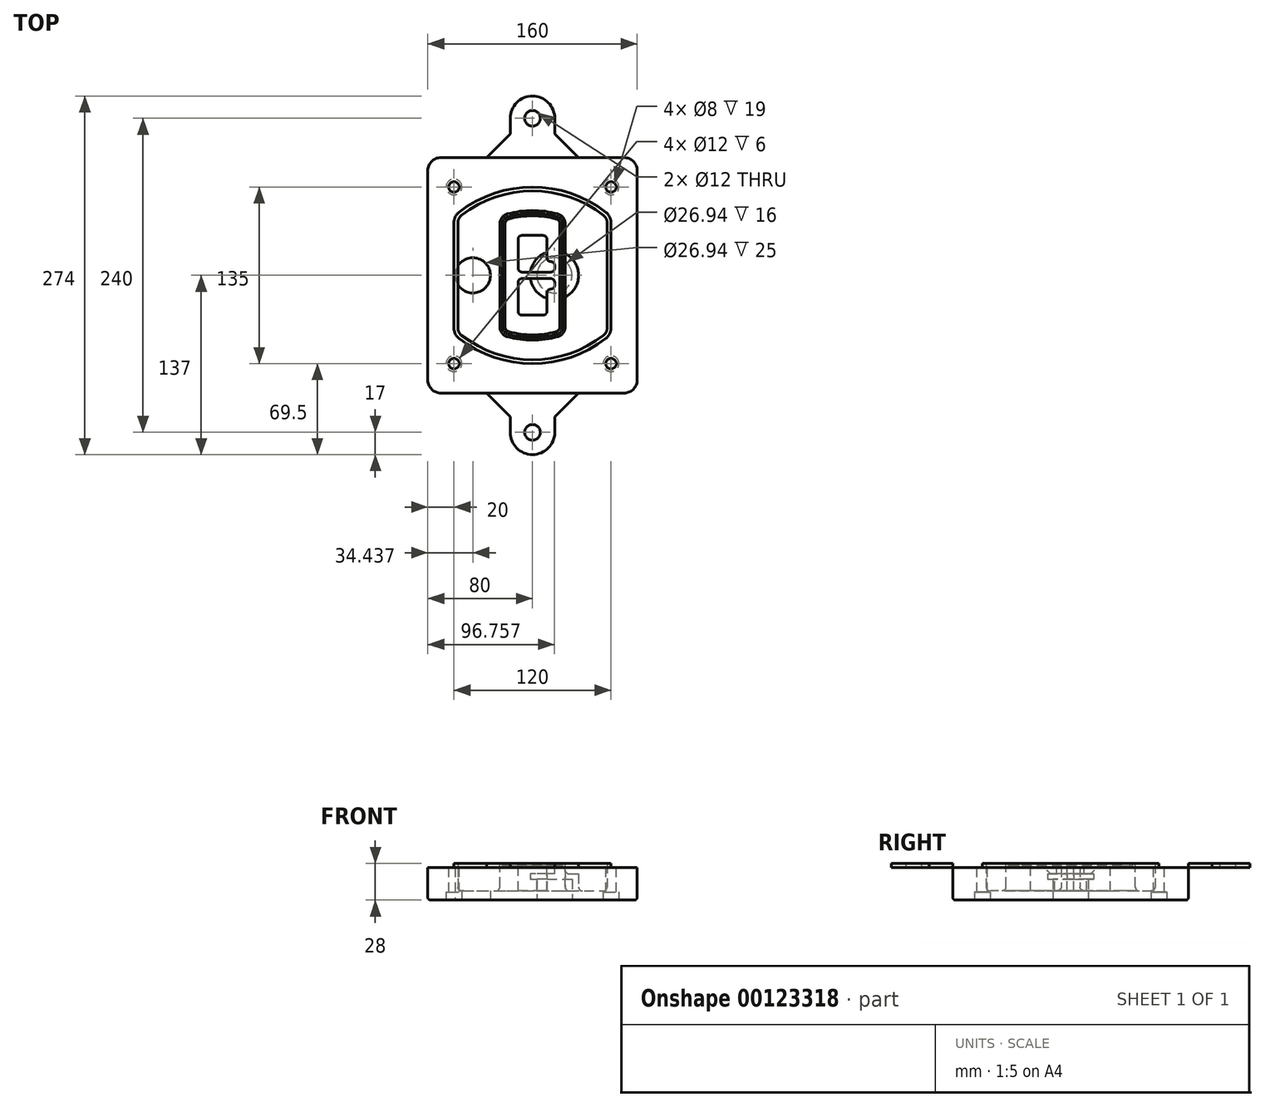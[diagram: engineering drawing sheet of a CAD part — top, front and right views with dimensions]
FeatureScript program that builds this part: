
annotation { "Feature Type Name" : "Feature", "Feature Type Description" : "" }
export const myFeature = defineFeature(function(context is Context, id is Id, definition is map)
    precondition{}
    {
        {
            var Q0;
            Q0=qCreatedBy(makeId("Top.planeOp"),FACE);
            var sketch = newSketch(context, id + "F0", { "sketchPlane" : qUnion([Q0])});
            skPoint(sketch, "E0.rect.middle", {"position": v(0, 0) * mm});
            skLineSegment(sketch, "E1.bottom", {"start": v(-70, -90) * mm, "end": v(70, -90) * mm});
            skLineSegment(sketch, "E1.top", {"start": v(-70, 90) * mm, "end": v(70, 90) * mm});
            skLineSegment(sketch, "E1.left", {"start": v(-80, -80) * mm, "end": v(-80, 80) * mm});
            skLineSegment(sketch, "E1.right", {"start": v(80, -80) * mm, "end": v(80, 80) * mm});
            skLineSegment(sketch, "E2", {"start": v(-80, 90) * mm, "end": v(80, -90) * mm, "construction": true});
            skLineSegment(sketch, "E3", {"start": v(80, 90) * mm, "end": v(-80, -90) * mm, "construction": true});
            skCircle(sketch, "E4", {"center": v(-60, 67.5) * mm, "radius": 4 * mm});
            skCircle(sketch, "E5", {"center": v(60, 67.5) * mm, "radius": 4 * mm});
            skCircle(sketch, "E6", {"center": v(60, -67.5) * mm, "radius": 4 * mm});
            skCircle(sketch, "E7", {"center": v(-60, -67.5) * mm, "radius": 4 * mm});
            skLineSegment(sketch, "E8", {"start": v(-60, 67.5) * mm, "end": v(60, 67.5) * mm, "construction": true});
            skLineSegment(sketch, "E9", {"start": v(60, 67.5) * mm, "end": v(60, -67.5) * mm, "construction": true});
            skLineSegment(sketch, "E10", {"start": v(60, -67.5) * mm, "end": v(-60, -67.5) * mm, "construction": true});
            skLineSegment(sketch, "E11", {"start": v(-60, -67.5) * mm, "end": v(-60, 67.5) * mm, "construction": true});
            skLineSegment(sketch, "E12", {"start": v(-60, 40.3) * mm, "end": v(-60, -40.3) * mm});
            skLineSegment(sketch, "E13", {"start": v(60, 40.3) * mm, "end": v(60, -40.3) * mm});
            skArc(sketch, "E14", {"start": v(56.15, 48.18) * mm, "mid": v(0, 67.5) * mm, "end": v(-56.15, 48.18) * mm});
            skArc(sketch, "E15", {"start": v(-56.15, -48.18) * mm, "mid": v(0, -67.5) * mm, "end": v(56.15, -48.18) * mm});
            skLineSegment(sketch, "E16", {"start": v(-60, 0) * mm, "end": v(60, 0) * mm, "construction": true});
            skPoint(sketch, "E17.visualSharp", {"position": v(-60, -45) * mm});
            skArc(sketch, "E17.filletArc", {"start": v(-60, -40.3) * mm, "mid": v(-58.99, -44.68) * mm, "end": v(-56.15, -48.18) * mm});
            skPoint(sketch, "E18.visualSharp", {"position": v(-60, 45) * mm});
            skArc(sketch, "E18.filletArc", {"start": v(-56.15, 48.18) * mm, "mid": v(-58.99, 44.68) * mm, "end": v(-60, 40.3) * mm});
            skPoint(sketch, "E19.visualSharp", {"position": v(60, 45) * mm});
            skArc(sketch, "E19.filletArc", {"start": v(60, 40.3) * mm, "mid": v(58.99, 44.68) * mm, "end": v(56.15, 48.18) * mm});
            skPoint(sketch, "E20.visualSharp", {"position": v(60, -45) * mm});
            skArc(sketch, "E20.filletArc", {"start": v(56.15, -48.18) * mm, "mid": v(58.99, -44.68) * mm, "end": v(60, -40.3) * mm});
            skPoint(sketch, "E21.visualSharp", {"position": v(-80, 90) * mm});
            skArc(sketch, "E21.filletArc", {"start": v(-70, 90) * mm, "mid": v(-77.07, 87.07) * mm, "end": v(-80, 80) * mm});
            skPoint(sketch, "E22.visualSharp", {"position": v(80, 90) * mm});
            skArc(sketch, "E22.filletArc", {"start": v(80, 80) * mm, "mid": v(77.07, 87.07) * mm, "end": v(70, 90) * mm});
            skPoint(sketch, "E23.visualSharp", {"position": v(80, -90) * mm});
            skArc(sketch, "E23.filletArc", {"start": v(70, -90) * mm, "mid": v(77.07, -87.07) * mm, "end": v(80, -80) * mm});
            skPoint(sketch, "E24.visualSharp", {"position": v(-80, -90) * mm});
            skArc(sketch, "E24.filletArc", {"start": v(-80, -80) * mm, "mid": v(-77.07, -87.07) * mm, "end": v(-70, -90) * mm});
            skArc(sketch, "E25.0", {"start": v(57, 40.3) * mm, "mid": v(56.3, 43.36) * mm, "end": v(54.3, 45.81) * mm});
            skLineSegment(sketch, "E25.1", {"start": v(57, 40.3) * mm, "end": v(57, -40.3) * mm});
            skArc(sketch, "E25.2", {"start": v(54.3, -45.81) * mm, "mid": v(56.3, -43.36) * mm, "end": v(57, -40.3) * mm});
            skArc(sketch, "E25.3", {"start": v(-54.3, -45.81) * mm, "mid": v(0, -64.5) * mm, "end": v(54.3, -45.81) * mm});
            skArc(sketch, "E25.4", {"start": v(-57, -40.3) * mm, "mid": v(-56.3, -43.36) * mm, "end": v(-54.3, -45.81) * mm});
            skArc(sketch, "E25.5", {"start": v(54.3, 45.81) * mm, "mid": v(0, 64.5) * mm, "end": v(-54.3, 45.81) * mm});
            skLineSegment(sketch, "E25.6", {"start": v(-57, 40.3) * mm, "end": v(-57, -40.3) * mm});
            skArc(sketch, "E25.7", {"start": v(-54.3, 45.81) * mm, "mid": v(-56.3, 43.36) * mm, "end": v(-57, 40.3) * mm});
            skArc(sketch, "E26.0", {"start": v(-58.62, 51.33) * mm, "mid": v(-62.58, 46.43) * mm, "end": v(-64, 40.3) * mm});
            skArc(sketch, "E26.1", {"start": v(58.62, 51.33) * mm, "mid": v(0, 71.5) * mm, "end": v(-58.62, 51.33) * mm});
            skArc(sketch, "E26.2", {"start": v(64, 40.3) * mm, "mid": v(62.58, 46.43) * mm, "end": v(58.62, 51.33) * mm});
            skLineSegment(sketch, "E26.3", {"start": v(64, 40.3) * mm, "end": v(64, -40.3) * mm});
            skArc(sketch, "E26.4", {"start": v(58.62, -51.33) * mm, "mid": v(62.58, -46.43) * mm, "end": v(64, -40.3) * mm});
            skLineSegment(sketch, "E26.5", {"start": v(-64, 40.3) * mm, "end": v(-64, -40.3) * mm});
            skArc(sketch, "E26.6", {"start": v(-58.62, -51.33) * mm, "mid": v(0, -71.5) * mm, "end": v(58.62, -51.33) * mm});
            skArc(sketch, "E26.7", {"start": v(-64, -40.3) * mm, "mid": v(-62.58, -46.43) * mm, "end": v(-58.62, -51.33) * mm});
            skSolve(sketch);
        }
        {
            var Q0;
            Q0=makeQuery(id+"F0.imprint","IMPRINT",FACE,{"disambiguationData":[TD([[makeQuery(id+"F0.imprint","IMPRINT",EDGE,{"derivedFrom":sQuery(id+"F0.wireOp",EDGE,"E1.bottom")}),1.0]])]});
            var Q1;
            Q1=makeQuery(id+"F0.imprint","IMPRINT",FACE,{"disambiguationData":[TD([[makeQuery(id+"F0.imprint","IMPRINT",EDGE,{"derivedFrom":sQuery(id+"F0.wireOp",EDGE,"E12")}),1.0]])]});
            var Q2;
            Q2=makeQuery(id+"F0.imprint","IMPRINT",FACE,{"disambiguationData":[TD([[makeQuery(id+"F0.imprint","IMPRINT",EDGE,{"derivedFrom":sQuery(id+"F0.wireOp",EDGE,"E25.0")}),1.0]])]});
            var Q3;
            Q3=makeQuery(id+"F0.imprint","IMPRINT",FACE,{"disambiguationData":[TD([[makeQuery(id+"F0.imprint","IMPRINT",EDGE,{"derivedFrom":sQuery(id+"F0.wireOp",EDGE,"E12")}),-1.0]])]});
            extrude(context, id + "F1", {"entities" : qUnion([Q0, Q1, Q2, Q3]), "oppositeDirection" : true, "depth" : 25 * mm});
        }
        {
            var Q0;
            Q0=makeQuery(id+"F0.imprint","IMPRINT",FACE,{"disambiguationData":[TD([[makeQuery(id+"F0.imprint","IMPRINT",EDGE,{"derivedFrom":sQuery(id+"F0.wireOp",EDGE,"E12")}),1.0]])]});
            extrude(context, id + "F2", {"entities" : qUnion([Q0]), "operationType" : NewBodyOperationType.ADD, "depth" : 3 * mm});
        }
        {
            var Q0;
            Q0=makeQuery(id+"F0.imprint","IMPRINT",FACE,{"disambiguationData":[TD([[makeQuery(id+"F0.imprint","IMPRINT",EDGE,{"derivedFrom":sQuery(id+"F0.wireOp",EDGE,"E25.0")}),1.0]])]});
            extrude(context, id + "F3", {"entities" : qUnion([Q0]), "operationType" : NewBodyOperationType.REMOVE, "oppositeDirection" : true, "depth" : 18 * mm});
        }
        {
            var Q0;
            Q0=makeQuery(id+"F2.opExtrude","CAP_FACE",FACE,{"disambiguationData":[OSD([sQuery(id+"F0.wireOp",EDGE,"E12"),sQuery(id+"F0.wireOp",EDGE,"E13"),sQuery(id+"F0.wireOp",EDGE,"E14"),sQuery(id+"F0.wireOp",EDGE,"E15"),sQuery(id+"F0.wireOp",EDGE,"E17.filletArc"),sQuery(id+"F0.wireOp",EDGE,"E18.filletArc"),sQuery(id+"F0.wireOp",EDGE,"E19.filletArc"),sQuery(id+"F0.wireOp",EDGE,"E20.filletArc"),sQuery(id+"F0.wireOp",EDGE,"E25.0"),sQuery(id+"F0.wireOp",EDGE,"E25.1"),sQuery(id+"F0.wireOp",EDGE,"E25.2"),sQuery(id+"F0.wireOp",EDGE,"E25.3"),sQuery(id+"F0.wireOp",EDGE,"E25.4"),sQuery(id+"F0.wireOp",EDGE,"E25.5"),sQuery(id+"F0.wireOp",EDGE,"E25.6"),sQuery(id+"F0.wireOp",EDGE,"E25.7")])],"isStart":false});
            var sketch = newSketch(context, id + "F4", { "sketchPlane" : qUnion([Q0])});
            skArc(sketch, "E27.0", {"start": v(-19.08, -46.97) * mm, "mid": v(0, -49.5) * mm, "end": v(19.08, -46.97) * mm});
            skArc(sketch, "E28.0", {"start": v(19.08, 46.97) * mm, "mid": v(0, 49.5) * mm, "end": v(-19.08, 46.97) * mm});
            skLineSegment(sketch, "E29", {"start": v(-25, 39.25) * mm, "end": v(-25, -39.25) * mm});
            skLineSegment(sketch, "E30", {"start": v(25, 39.25) * mm, "end": v(25, -39.25) * mm});
            skLineSegment(sketch, "E31", {"start": v(-25, 45.1) * mm, "end": v(25, 45.1) * mm, "construction": true});
            skLineSegment(sketch, "E32", {"start": v(-25, -45.1) * mm, "end": v(25, -45.1) * mm, "construction": true});
            skPoint(sketch, "E33.visualSharp", {"position": v(-25, 45.1) * mm});
            skArc(sketch, "E33.filletArc", {"start": v(-19.08, 46.97) * mm, "mid": v(-23.35, 44.11) * mm, "end": v(-25, 39.25) * mm});
            skPoint(sketch, "E34.visualSharp", {"position": v(25, 45.1) * mm});
            skArc(sketch, "E34.filletArc", {"start": v(25, 39.25) * mm, "mid": v(23.35, 44.11) * mm, "end": v(19.08, 46.97) * mm});
            skPoint(sketch, "E35.visualSharp", {"position": v(25, -45.1) * mm});
            skArc(sketch, "E35.filletArc", {"start": v(19.08, -46.97) * mm, "mid": v(23.35, -44.11) * mm, "end": v(25, -39.25) * mm});
            skPoint(sketch, "E36.visualSharp", {"position": v(-25, -45.1) * mm});
            skArc(sketch, "E36.filletArc", {"start": v(-25, -39.25) * mm, "mid": v(-23.35, -44.11) * mm, "end": v(-19.08, -46.97) * mm});
            skArc(sketch, "E37.0", {"start": v(54.3, 45.81) * mm, "mid": v(0, 64.5) * mm, "end": v(-54.3, 45.81) * mm});
            skArc(sketch, "E37.1", {"start": v(-54.3, 45.81) * mm, "mid": v(-56.3, 43.36) * mm, "end": v(-57, 40.3) * mm});
            skLineSegment(sketch, "E37.2", {"start": v(-57, 40.3) * mm, "end": v(-57, -40.3) * mm});
            skArc(sketch, "E37.3", {"start": v(-57, -40.3) * mm, "mid": v(-56.3, -43.36) * mm, "end": v(-54.3, -45.81) * mm});
            skArc(sketch, "E37.4", {"start": v(-54.3, -45.81) * mm, "mid": v(0, -64.5) * mm, "end": v(54.3, -45.81) * mm});
            skArc(sketch, "E37.5", {"start": v(54.3, -45.81) * mm, "mid": v(56.3, -43.36) * mm, "end": v(57, -40.3) * mm});
            skLineSegment(sketch, "E37.6", {"start": v(57, 40.3) * mm, "end": v(57, -40.3) * mm});
            skArc(sketch, "E37.7", {"start": v(57, 40.3) * mm, "mid": v(56.3, 43.36) * mm, "end": v(54.3, 45.81) * mm});
            skLineSegment(sketch, "E38.0", {"start": v(23, 39.25) * mm, "end": v(23, -39.25) * mm});
            skArc(sketch, "E38.1", {"start": v(18.56, -45.04) * mm, "mid": v(21.76, -42.9) * mm, "end": v(23, -39.25) * mm});
            skArc(sketch, "E38.2", {"start": v(-18.56, -45.04) * mm, "mid": v(0, -47.5) * mm, "end": v(18.56, -45.04) * mm});
            skArc(sketch, "E38.3", {"start": v(-23, -39.25) * mm, "mid": v(-21.76, -42.9) * mm, "end": v(-18.56, -45.04) * mm});
            skLineSegment(sketch, "E38.4", {"start": v(-23, 39.25) * mm, "end": v(-23, -39.25) * mm});
            skArc(sketch, "E38.5", {"start": v(23, 39.25) * mm, "mid": v(21.76, 42.9) * mm, "end": v(18.56, 45.04) * mm});
            skArc(sketch, "E38.6", {"start": v(-18.56, 45.04) * mm, "mid": v(-21.76, 42.9) * mm, "end": v(-23, 39.25) * mm});
            skArc(sketch, "E38.7", {"start": v(18.56, 45.04) * mm, "mid": v(0, 47.5) * mm, "end": v(-18.56, 45.04) * mm});
            skArc(sketch, "E39.0", {"start": v(21, 39.25) * mm, "mid": v(20.18, 41.68) * mm, "end": v(18.04, 43.1) * mm});
            skLineSegment(sketch, "E39.1", {"start": v(21, 39.25) * mm, "end": v(21, -39.25) * mm});
            skArc(sketch, "E39.2", {"start": v(18.04, -43.1) * mm, "mid": v(20.18, -41.68) * mm, "end": v(21, -39.25) * mm});
            skArc(sketch, "E39.3", {"start": v(-18.04, -43.1) * mm, "mid": v(0, -45.5) * mm, "end": v(18.04, -43.1) * mm});
            skArc(sketch, "E39.4", {"start": v(-21, -39.25) * mm, "mid": v(-20.18, -41.68) * mm, "end": v(-18.04, -43.1) * mm});
            skArc(sketch, "E39.5", {"start": v(18.04, 43.1) * mm, "mid": v(0, 45.5) * mm, "end": v(-18.04, 43.1) * mm});
            skLineSegment(sketch, "E39.6", {"start": v(-21, 39.25) * mm, "end": v(-21, -39.25) * mm});
            skArc(sketch, "E39.7", {"start": v(-18.04, 43.1) * mm, "mid": v(-20.18, 41.68) * mm, "end": v(-21, 39.25) * mm});
            skLineSegment(sketch, "E40", {"start": v(-25, 0) * mm, "end": v(25, 0) * mm, "construction": true});
            skLineSegment(sketch, "E41", {"start": v(-11, 5.5) * mm, "end": v(-11, 27.5) * mm});
            skLineSegment(sketch, "E42", {"start": v(-8, 30.5) * mm, "end": v(8, 30.5) * mm});
            skLineSegment(sketch, "E43", {"start": v(11, 27.5) * mm, "end": v(11, 13.5) * mm});
            skLineSegment(sketch, "E44", {"start": v(14, 10.5) * mm, "end": v(14, 10.5) * mm});
            skLineSegment(sketch, "E45", {"start": v(17, 7.5) * mm, "end": v(17, 5.5) * mm});
            skLineSegment(sketch, "E46", {"start": v(14, 2.5) * mm, "end": v(-8, 2.5) * mm});
            skPoint(sketch, "E47.visualSharp", {"position": v(-11, 30.5) * mm});
            skArc(sketch, "E47.filletArc", {"start": v(-8, 30.5) * mm, "mid": v(-10.12, 29.62) * mm, "end": v(-11, 27.5) * mm});
            skPoint(sketch, "E48.visualSharp", {"position": v(11, 30.5) * mm});
            skArc(sketch, "E48.filletArc", {"start": v(11, 27.5) * mm, "mid": v(10.12, 29.62) * mm, "end": v(8, 30.5) * mm});
            skPoint(sketch, "E49.visualSharp", {"position": v(11, 10.5) * mm});
            skArc(sketch, "E49.filletArc", {"start": v(11, 13.5) * mm, "mid": v(11.88, 11.38) * mm, "end": v(14, 10.5) * mm});
            skPoint(sketch, "E50.visualSharp", {"position": v(17, 10.5) * mm});
            skArc(sketch, "E50.filletArc", {"start": v(17, 7.5) * mm, "mid": v(16.12, 9.62) * mm, "end": v(14, 10.5) * mm});
            skPoint(sketch, "E51.visualSharp", {"position": v(17, 2.5) * mm});
            skArc(sketch, "E51.filletArc", {"start": v(14, 2.5) * mm, "mid": v(16.12, 3.38) * mm, "end": v(17, 5.5) * mm});
            skPoint(sketch, "E52.visualSharp", {"position": v(-11, 2.5) * mm});
            skArc(sketch, "E52.filletArc", {"start": v(-11, 5.5) * mm, "mid": v(-10.12, 3.38) * mm, "end": v(-8, 2.5) * mm});
            skLineSegment(sketch, "E53.0.MirrorCS", {"start": v(14, -2.5) * mm, "end": v(-8, -2.5) * mm});
            skArc(sketch, "E54.0.MirrorCS", {"start": v(-11, -5.5) * mm, "mid": v(-10.12, -3.38) * mm, "end": v(-8, -2.5) * mm});
            skLineSegment(sketch, "E55.0.MirrorCS", {"start": v(-11, -5.5) * mm, "end": v(-11, -27.5) * mm});
            skArc(sketch, "E56.0.MirrorCS", {"start": v(-8, -30.5) * mm, "mid": v(-10.12, -29.62) * mm, "end": v(-11, -27.5) * mm});
            skLineSegment(sketch, "E57.0.MirrorCS", {"start": v(-8, -30.5) * mm, "end": v(8, -30.5) * mm});
            skArc(sketch, "E58.0.MirrorCS", {"start": v(11, -27.5) * mm, "mid": v(10.12, -29.62) * mm, "end": v(8, -30.5) * mm});
            skLineSegment(sketch, "E59.0.MirrorCS", {"start": v(11, -27.5) * mm, "end": v(11, -13.5) * mm});
            skArc(sketch, "E60.0.MirrorCS", {"start": v(11, -13.5) * mm, "mid": v(11.88, -11.38) * mm, "end": v(14, -10.5) * mm});
            skArc(sketch, "E61.0.MirrorCS", {"start": v(17, -7.5) * mm, "mid": v(16.12, -9.62) * mm, "end": v(14, -10.5) * mm});
            skLineSegment(sketch, "E62.0.MirrorCS", {"start": v(17, -7.5) * mm, "end": v(17, -5.5) * mm});
            skArc(sketch, "E63.0.MirrorCS", {"start": v(14, -2.5) * mm, "mid": v(16.12, -3.38) * mm, "end": v(17, -5.5) * mm});
            skSolve(sketch);
        }
        {
            var Q0;
            Q0=makeQuery(id+"F4.imprint","IMPRINT",FACE,{"disambiguationData":[TD([[makeQuery(id+"F4.imprint","IMPRINT",EDGE,{"derivedFrom":sQuery(id+"F4.wireOp",EDGE,"E27.0")}),1.0]])]});
            var Q1;
            Q1=makeQuery(id+"F4.imprint","IMPRINT",FACE,{"disambiguationData":[TD([[makeQuery(id+"F4.imprint","IMPRINT",EDGE,{"derivedFrom":sQuery(id+"F4.wireOp",EDGE,"E38.0")}),-1.0]])]});
            var Q2;
            Q2=makeQuery(id+"F4.imprint","IMPRINT",FACE,{"disambiguationData":[TD([[makeQuery(id+"F4.imprint","IMPRINT",EDGE,{"derivedFrom":sQuery(id+"F4.wireOp",EDGE,"E39.0")}),1.0]])]});
            extrude(context, id + "F5", {"entities" : qUnion([Q0, Q1, Q2]), "operationType" : NewBodyOperationType.ADD, "endBound" : BoundingType.UP_TO_NEXT, "oppositeDirection" : true, "depth" : 25 * mm});
        }
        {
            var Q0;
            Q0=makeQuery(id+"F4.imprint","IMPRINT",FACE,{"disambiguationData":[TD([[makeQuery(id+"F4.imprint","IMPRINT",EDGE,{"derivedFrom":sQuery(id+"F4.wireOp",EDGE,"E38.0")}),-1.0]])]});
            extrude(context, id + "F6", {"entities" : qUnion([Q0]), "operationType" : NewBodyOperationType.REMOVE, "oppositeDirection" : true, "depth" : 2 * mm});
        }
        {
            var Q0;
            Q0=makeQuery(id+"F1.opExtrude","CAP_FACE",FACE,{"disambiguationData":[OSD([sQuery(id+"F0.wireOp",EDGE,"E1.bottom"),sQuery(id+"F0.wireOp",EDGE,"E1.top"),sQuery(id+"F0.wireOp",EDGE,"E1.left"),sQuery(id+"F0.wireOp",EDGE,"E1.right"),sQuery(id+"F0.wireOp",EDGE,"E4"),sQuery(id+"F0.wireOp",EDGE,"E5"),sQuery(id+"F0.wireOp",EDGE,"E6"),sQuery(id+"F0.wireOp",EDGE,"E7"),sQuery(id+"F0.wireOp",EDGE,"E21.filletArc"),sQuery(id+"F0.wireOp",EDGE,"E22.filletArc"),sQuery(id+"F0.wireOp",EDGE,"E23.filletArc"),sQuery(id+"F0.wireOp",EDGE,"E24.filletArc")])],"isStart":false});
            var sketch = newSketch(context, id + "F7", { "sketchPlane" : qUnion([Q0])});
            skCircle(sketch, "E64", {"center": v(16.76, 0) * mm, "radius": 13.47 * mm});
            skCircle(sketch, "E65", {"center": v(-45.56, 0) * mm, "radius": 13.47 * mm});
            skLineSegment(sketch, "E66", {"start": v(80, 0) * mm, "end": v(-80, 0) * mm});
            skCircle(sketch, "E67", {"center": v(16.76, 0) * mm, "radius": 18.47 * mm});
            skCircle(sketch, "E68", {"center": v(60, -67.5) * mm, "radius": 6 * mm});
            skCircle(sketch, "E69", {"center": v(-60, -67.5) * mm, "radius": 6 * mm});
            skCircle(sketch, "E70", {"center": v(-60, 67.5) * mm, "radius": 6 * mm});
            skCircle(sketch, "E71", {"center": v(60, 67.5) * mm, "radius": 6 * mm});
            skSolve(sketch);
        }
        {
            var Q0;
            {var subQ1=sQuery(id+"F7.wireOp",EDGE,"E66");var subQ4=sQuery(id+"F7.wireOp",EDGE,"E64");var subQ6=makeQuery(id+"F7.imprint","INTERSECT",VERTEX,{"disambiguationData":[OD(0.0)],"derivedFrom":[subQ4,subQ1]});Q0=makeQuery(id+"F7.imprint","IMPRINT",FACE,{"disambiguationData":[TD([[makeQuery(id+"F7.imprint","IMPRINT",EDGE,{"disambiguationData":[TD([[subQ6,-1.0]])],"derivedFrom":subQ4}),-1.0]])]});}
            var Q1;
            {var subQ0=sQuery(id+"F7.wireOp",EDGE,"E66");var subQ1=sQuery(id+"F7.wireOp",EDGE,"E64");var subQ3=makeQuery(id+"F7.imprint","INTERSECT",VERTEX,{"disambiguationData":[OD(0.0)],"derivedFrom":[subQ1,subQ0]});Q1=makeQuery(id+"F7.imprint","IMPRINT",FACE,{"disambiguationData":[TD([[makeQuery(id+"F7.imprint","IMPRINT",EDGE,{"disambiguationData":[TD([[subQ3,-1.0]])],"derivedFrom":subQ1}),1.0]])]});}
            var Q2;
            {var subQ0=sQuery(id+"F7.wireOp",EDGE,"E66");var subQ1=sQuery(id+"F7.wireOp",EDGE,"E64");var subQ3=makeQuery(id+"F7.imprint","INTERSECT",VERTEX,{"disambiguationData":[OD(0.0)],"derivedFrom":[subQ1,subQ0]});Q2=makeQuery(id+"F7.imprint","IMPRINT",FACE,{"disambiguationData":[TD([[makeQuery(id+"F7.imprint","IMPRINT",EDGE,{"disambiguationData":[TD([[subQ3,1.0]])],"derivedFrom":subQ1}),1.0]])]});}
            var Q3;
            {var subQ1=sQuery(id+"F7.wireOp",EDGE,"E66");var subQ4=sQuery(id+"F7.wireOp",EDGE,"E64");var subQ6=makeQuery(id+"F7.imprint","INTERSECT",VERTEX,{"disambiguationData":[OD(0.0)],"derivedFrom":[subQ4,subQ1]});Q3=makeQuery(id+"F7.imprint","IMPRINT",FACE,{"disambiguationData":[TD([[makeQuery(id+"F7.imprint","IMPRINT",EDGE,{"disambiguationData":[TD([[subQ6,1.0]])],"derivedFrom":subQ4}),-1.0]])]});}
            extrude(context, id + "F8", {"entities" : qUnion([Q0, Q1, Q2, Q3]), "operationType" : NewBodyOperationType.ADD, "oppositeDirection" : true, "depth" : 20 * mm});
        }
        {
            var Q0;
            {var subQ0=sQuery(id+"F7.wireOp",EDGE,"E66");var subQ1=sQuery(id+"F7.wireOp",EDGE,"E64");var subQ3=makeQuery(id+"F7.imprint","INTERSECT",VERTEX,{"disambiguationData":[OD(0.0)],"derivedFrom":[subQ1,subQ0]});Q0=makeQuery(id+"F7.imprint","IMPRINT",FACE,{"disambiguationData":[TD([[makeQuery(id+"F7.imprint","IMPRINT",EDGE,{"disambiguationData":[TD([[subQ3,-1.0]])],"derivedFrom":subQ1}),1.0]])]});}
            var Q1;
            {var subQ0=sQuery(id+"F7.wireOp",EDGE,"E66");var subQ1=sQuery(id+"F7.wireOp",EDGE,"E64");var subQ3=makeQuery(id+"F7.imprint","INTERSECT",VERTEX,{"disambiguationData":[OD(0.0)],"derivedFrom":[subQ1,subQ0]});Q1=makeQuery(id+"F7.imprint","IMPRINT",FACE,{"disambiguationData":[TD([[makeQuery(id+"F7.imprint","IMPRINT",EDGE,{"disambiguationData":[TD([[subQ3,1.0]])],"derivedFrom":subQ1}),1.0]])]});}
            extrude(context, id + "F9", {"entities" : qUnion([Q0, Q1]), "operationType" : NewBodyOperationType.REMOVE, "oppositeDirection" : true, "depth" : 16 * mm});
        }
        {
            var Q0;
            {var subQ0=sQuery(id+"F7.wireOp",EDGE,"E66");var subQ1=sQuery(id+"F7.wireOp",EDGE,"E65");var subQ3=makeQuery(id+"F7.imprint","INTERSECT",VERTEX,{"disambiguationData":[OD(0.0)],"derivedFrom":[subQ1,subQ0]});Q0=makeQuery(id+"F7.imprint","IMPRINT",FACE,{"disambiguationData":[TD([[makeQuery(id+"F7.imprint","IMPRINT",EDGE,{"disambiguationData":[TD([[subQ3,-1.0]])],"derivedFrom":subQ1}),1.0]])]});}
            var Q1;
            {var subQ0=sQuery(id+"F7.wireOp",EDGE,"E66");var subQ1=sQuery(id+"F7.wireOp",EDGE,"E65");var subQ3=makeQuery(id+"F7.imprint","INTERSECT",VERTEX,{"disambiguationData":[OD(0.0)],"derivedFrom":[subQ1,subQ0]});Q1=makeQuery(id+"F7.imprint","IMPRINT",FACE,{"disambiguationData":[TD([[makeQuery(id+"F7.imprint","IMPRINT",EDGE,{"disambiguationData":[TD([[subQ3,1.0]])],"derivedFrom":subQ1}),1.0]])]});}
            extrude(context, id + "F10", {"entities" : qUnion([Q0, Q1]), "operationType" : NewBodyOperationType.REMOVE, "oppositeDirection" : true, "depth" : 25 * mm});
        }
        {
            var Q0;
            Q0=makeQuery(id+"F7.imprint","IMPRINT",FACE,{"disambiguationData":[TD([[makeQuery(id+"F7.imprint","IMPRINT",EDGE,{"derivedFrom":sQuery(id+"F7.wireOp",EDGE,"E68")}),1.0]])]});
            var Q1;
            Q1=makeQuery(id+"F7.imprint","IMPRINT",FACE,{"disambiguationData":[TD([[makeQuery(id+"F7.imprint","IMPRINT",EDGE,{"derivedFrom":makeQuery(id+"F1.opExtrude","CAP_EDGE",EDGE,{"disambiguationData":[OSD([sQuery(id+"F0.wireOp",EDGE,"E5")])],"isStart":false})}),-1.0]])]});
            var Q2;
            Q2=makeQuery(id+"F7.imprint","IMPRINT",FACE,{"disambiguationData":[TD([[makeQuery(id+"F7.imprint","IMPRINT",EDGE,{"derivedFrom":sQuery(id+"F7.wireOp",EDGE,"E69")}),1.0]])]});
            var Q3;
            Q3=makeQuery(id+"F7.imprint","IMPRINT",FACE,{"disambiguationData":[TD([[makeQuery(id+"F7.imprint","IMPRINT",EDGE,{"derivedFrom":makeQuery(id+"F1.opExtrude","CAP_EDGE",EDGE,{"disambiguationData":[OSD([sQuery(id+"F0.wireOp",EDGE,"E4")])],"isStart":false})}),-1.0]])]});
            var Q4;
            Q4=makeQuery(id+"F7.imprint","IMPRINT",FACE,{"disambiguationData":[TD([[makeQuery(id+"F7.imprint","IMPRINT",EDGE,{"derivedFrom":sQuery(id+"F7.wireOp",EDGE,"E70")}),1.0]])]});
            var Q5;
            Q5=makeQuery(id+"F7.imprint","IMPRINT",FACE,{"disambiguationData":[TD([[makeQuery(id+"F7.imprint","IMPRINT",EDGE,{"derivedFrom":makeQuery(id+"F1.opExtrude","CAP_EDGE",EDGE,{"disambiguationData":[OSD([sQuery(id+"F0.wireOp",EDGE,"E7")])],"isStart":false})}),-1.0]])]});
            var Q6;
            Q6=makeQuery(id+"F7.imprint","IMPRINT",FACE,{"disambiguationData":[TD([[makeQuery(id+"F7.imprint","IMPRINT",EDGE,{"derivedFrom":sQuery(id+"F7.wireOp",EDGE,"E71")}),1.0]])]});
            var Q7;
            Q7=makeQuery(id+"F7.imprint","IMPRINT",FACE,{"disambiguationData":[TD([[makeQuery(id+"F7.imprint","IMPRINT",EDGE,{"derivedFrom":makeQuery(id+"F1.opExtrude","CAP_EDGE",EDGE,{"disambiguationData":[OSD([sQuery(id+"F0.wireOp",EDGE,"E6")])],"isStart":false})}),-1.0]])]});
            extrude(context, id + "F11", {"entities" : qUnion([Q0, Q1, Q2, Q3, Q4, Q5, Q6, Q7]), "operationType" : NewBodyOperationType.REMOVE, "oppositeDirection" : true, "depth" : 6 * mm});
        }
        {
            var Q0;
            Q0=makeQuery(id+"F9.boolean.opBoolean","COPY",FACE,{"derivedFrom":makeQuery(id+"F9.opExtrude","CAP_FACE",FACE,{"disambiguationData":[OSD([sQuery(id+"F7.wireOp",EDGE,"E64")])],"isStart":false})});
            var sketch = newSketch(context, id + "F12", { "sketchPlane" : qUnion([Q0])});
            skArc(sketch, "E72.0", {"start": v(11, 17.55) * mm, "mid": v(2.57, 11.82) * mm, "end": v(-1.54, 2.5) * mm});
            skArc(sketch, "E72.1", {"start": v(-1.54, -2.5) * mm, "mid": v(2.57, -11.82) * mm, "end": v(11, -17.55) * mm});
            skLineSegment(sketch, "E73", {"start": v(-1.54, -2.5) * mm, "end": v(14, -2.5) * mm});
            skLineSegment(sketch, "E74.0", {"start": v(14, 2.5) * mm, "end": v(-1.54, 2.5) * mm});
            skArc(sketch, "E74.1", {"start": v(14, 2.5) * mm, "mid": v(16.12, 3.38) * mm, "end": v(17, 5.5) * mm});
            skLineSegment(sketch, "E74.2", {"start": v(17, 7.5) * mm, "end": v(17, 5.5) * mm});
            skArc(sketch, "E74.3", {"start": v(17, 7.5) * mm, "mid": v(16.12, 9.62) * mm, "end": v(14, 10.5) * mm});
            skArc(sketch, "E74.4", {"start": v(11, 13.5) * mm, "mid": v(11.88, 11.38) * mm, "end": v(14, 10.5) * mm});
            skLineSegment(sketch, "E74.5", {"start": v(11, 17.55) * mm, "end": v(11, 13.5) * mm});
            skLineSegment(sketch, "E74.7", {"start": v(14, -2.5) * mm, "end": v(-1.54, -2.5) * mm});
            skArc(sketch, "E74.8", {"start": v(14, -2.5) * mm, "mid": v(16.12, -3.38) * mm, "end": v(17, -5.5) * mm});
            skLineSegment(sketch, "E74.9", {"start": v(17, -7.5) * mm, "end": v(17, -5.5) * mm});
            skArc(sketch, "E74.10", {"start": v(17, -7.5) * mm, "mid": v(16.12, -9.62) * mm, "end": v(14, -10.5) * mm});
            skArc(sketch, "E74.11", {"start": v(11, -13.5) * mm, "mid": v(11.88, -11.38) * mm, "end": v(14, -10.5) * mm});
            skLineSegment(sketch, "E74.12", {"start": v(11, -17.55) * mm, "end": v(11, -13.5) * mm});
            skPoint(sketch, "E75.orphan", {"position": v(11, -27.5) * mm});
            skPoint(sketch, "E76.orphan", {"position": v(-8, -2.5) * mm});
            skPoint(sketch, "E77.orphan", {"position": v(-8, 2.5) * mm});
            skPoint(sketch, "E78.orphan", {"position": v(11, 27.5) * mm});
            skSolve(sketch);
        }
        {
            var Q0;
            {var subQ7=sQuery(id+"F12.wireOp",EDGE,"E72.0");var subQ14=sQuery(id+"F12.wireOp",EDGE,"E72.1");var subQ16=sQuery(id+"F12.wireOp",EDGE,"E74.1");var subQ18=sQuery(id+"F12.wireOp",EDGE,"E74.8");Q0=qUnion([makeQuery(id+"F12.imprint","IMPRINT",FACE,{"disambiguationData":[TD([[makeQuery(id+"F12.imprint","IMPRINT",EDGE,{"derivedFrom":subQ7}),1.0]])]}),makeQuery(id+"F12.imprint","IMPRINT",FACE,{"disambiguationData":[TD([[makeQuery(id+"F12.imprint","IMPRINT",EDGE,{"derivedFrom":subQ14}),1.0]])]}),makeQuery(id+"F12.imprint","IMPRINT",FACE,{"disambiguationData":[TD([[makeQuery(id+"F12.imprint","IMPRINT",EDGE,{"derivedFrom":subQ16}),1.0]])]}),makeQuery(id+"F12.imprint","IMPRINT",FACE,{"disambiguationData":[TD([[makeQuery(id+"F12.imprint","IMPRINT",EDGE,{"derivedFrom":subQ18}),-1.0]])]})]);}
            var Q1;
            Q1=makeQuery(id+"F5.boolean.opBoolean","SPLIT",FACE,{"disambiguationData":[TD([makeQuery(id+"F5.opExtrude","SWEPT_FACE",FACE,{"disambiguationData":[OSD([sQuery(id+"F4.wireOp",EDGE,"E41")])]})])],"derivedFrom":makeQuery(id+"F3.boolean.opBoolean","COPY",FACE,{"derivedFrom":makeQuery(id+"F3.opExtrude","CAP_FACE",FACE,{"disambiguationData":[OSD([sQuery(id+"F0.wireOp",EDGE,"E25.0"),sQuery(id+"F0.wireOp",EDGE,"E25.1"),sQuery(id+"F0.wireOp",EDGE,"E25.2"),sQuery(id+"F0.wireOp",EDGE,"E25.3"),sQuery(id+"F0.wireOp",EDGE,"E25.4"),sQuery(id+"F0.wireOp",EDGE,"E25.5"),sQuery(id+"F0.wireOp",EDGE,"E25.6"),sQuery(id+"F0.wireOp",EDGE,"E25.7")])],"isStart":false})})});
            extrude(context, id + "F13", {"entities" : qUnion([Q0]), "operationType" : NewBodyOperationType.REMOVE, "endBound" : BoundingType.UP_TO_SURFACE, "endBoundEntityFace" : qUnion([Q1]), "depth" : 25 * mm});
        }
        {
            var Q0;
            Q0=makeQuery(id+"F3.boolean.opBoolean","COPY",EDGE,{"derivedFrom":makeQuery(id+"F3.opExtrude","CAP_EDGE",EDGE,{"disambiguationData":[OSD([sQuery(id+"F0.wireOp",EDGE,"E25.6")])],"isStart":false})});
            var Q1;
            Q1=makeQuery(id+"F8.boolean.opBoolean","INTERSECT",EDGE,{"derivedFrom":[makeQuery(id+"F5.opExtrude","SWEPT_FACE",FACE,{"disambiguationData":[OSD([sQuery(id+"F4.wireOp",EDGE,"E30")])]}),makeQuery(id+"F8.opExtrude","CAP_FACE",FACE,{"disambiguationData":[OSD([sQuery(id+"F7.wireOp",EDGE,"E67")])],"isStart":false})]});
            var Q2;
            Q2=makeQuery(id+"F8.boolean.opBoolean","INTERSECT",EDGE,{"disambiguationData":[OD(1.0)],"derivedFrom":[makeQuery(id+"F5.opExtrude","SWEPT_FACE",FACE,{"disambiguationData":[OSD([sQuery(id+"F4.wireOp",EDGE,"E30")])]}),makeQuery(id+"F8.opExtrude","SWEPT_FACE",FACE,{"disambiguationData":[OSD([sQuery(id+"F7.wireOp",EDGE,"E67")])]})]});
            var Q3;
            {var subQ0=sQuery(id+"F4.wireOp",EDGE,"E30");Q3=makeQuery(id+"F8.boolean.opBoolean","SPLIT",EDGE,{"disambiguationData":[TD([makeQuery(id+"F5.opExtrude","SWEPT_FACE",FACE,{"disambiguationData":[OSD([sQuery(id+"F4.wireOp",EDGE,"E35.filletArc")])]})])],"derivedFrom":makeQuery(id+"F5.opExtrude","CAP_EDGE",EDGE,{"disambiguationData":[OSD([subQ0])],"isStart":false})});}
            var Q4;
            {var subQ0=sQuery(id+"F0.wireOp",EDGE,"E25.7");var subQ1=sQuery(id+"F0.wireOp",EDGE,"E25.1");var subQ2=sQuery(id+"F0.wireOp",EDGE,"E25.6");var subQ3=sQuery(id+"F0.wireOp",EDGE,"E25.5");var subQ4=sQuery(id+"F0.wireOp",EDGE,"E25.4");var subQ5=sQuery(id+"F0.wireOp",EDGE,"E25.0");var subQ6=sQuery(id+"F0.wireOp",EDGE,"E25.2");var subQ7=sQuery(id+"F0.wireOp",EDGE,"E25.3");Q4=makeQuery(id+"F8.boolean.opBoolean","INTERSECT",EDGE,{"derivedFrom":[makeQuery(id+"F5.boolean.opBoolean","SPLIT",FACE,{"disambiguationData":[TD([makeQuery(id+"F2.opExtrude","SWEPT_FACE",FACE,{"disambiguationData":[OSD([subQ5])]})])],"derivedFrom":makeQuery(id+"F3.boolean.opBoolean","COPY",FACE,{"derivedFrom":makeQuery(id+"F3.opExtrude","CAP_FACE",FACE,{"disambiguationData":[OSD([subQ5,subQ1,subQ6,subQ7,subQ4,subQ3,subQ2,subQ0])],"isStart":false})})}),makeQuery(id+"F8.opExtrude","SWEPT_FACE",FACE,{"disambiguationData":[OSD([sQuery(id+"F7.wireOp",EDGE,"E67")])]})]});}
            var Q5;
            Q5=makeQuery(id+"F8.boolean.opBoolean","INTERSECT",EDGE,{"disambiguationData":[OD(0.0)],"derivedFrom":[makeQuery(id+"F5.opExtrude","SWEPT_FACE",FACE,{"disambiguationData":[OSD([sQuery(id+"F4.wireOp",EDGE,"E30")])]}),makeQuery(id+"F8.opExtrude","SWEPT_FACE",FACE,{"disambiguationData":[OSD([sQuery(id+"F7.wireOp",EDGE,"E67")])]})]});
            fillet(context, id + "F14", {"entities" : qUnion([Q0, Q1, Q2, Q3, Q4, Q5]), "radius" : 3 * mm, "tangentPropagation" : true, "allowEdgeOverflow" : false});
        }
        {
            var Q0;
            Q0=makeQuery(id+"F1.opExtrude","CAP_EDGE",EDGE,{"disambiguationData":[OSD([sQuery(id+"F0.wireOp",EDGE,"E1.bottom")])],"isStart":false});
            fillet(context, id + "F15", {"entities" : qUnion([Q0]), "radius" : 2 * mm, "tangentPropagation" : true, "allowEdgeOverflow" : false});
        }
        {
            var Q0;
            {var subQ0=sQuery(id+"F0.wireOp",EDGE,"E22.filletArc");var subQ1=sQuery(id+"F0.wireOp",EDGE,"E7");var subQ2=sQuery(id+"F0.wireOp",EDGE,"E6");var subQ3=sQuery(id+"F0.wireOp",EDGE,"E5");var subQ4=sQuery(id+"F0.wireOp",EDGE,"E4");var subQ5=sQuery(id+"F0.wireOp",EDGE,"E1.bottom");var subQ6=sQuery(id+"F0.wireOp",EDGE,"E21.filletArc");var subQ7=sQuery(id+"F0.wireOp",EDGE,"E1.top");var subQ8=sQuery(id+"F0.wireOp",EDGE,"E1.left");var subQ9=sQuery(id+"F0.wireOp",EDGE,"E1.right");var subQ10=sQuery(id+"F0.wireOp",EDGE,"E23.filletArc");var subQ11=sQuery(id+"F0.wireOp",EDGE,"E24.filletArc");Q0=makeQuery(id+"F2.boolean.opBoolean","SPLIT",FACE,{"disambiguationData":[TD([makeQuery(id+"F1.opExtrude","SWEPT_FACE",FACE,{"disambiguationData":[OSD([subQ5])]})])],"derivedFrom":makeQuery(id+"F1.opExtrude","CAP_FACE",FACE,{"disambiguationData":[OSD([subQ5,subQ7,subQ8,subQ9,subQ4,subQ3,subQ2,subQ1,subQ6,subQ0,subQ10,subQ11])],"isStart":true})});}
            var sketch = newSketch(context, id + "F16", { "sketchPlane" : qUnion([Q0])});
            skLineSegment(sketch, "E79", {"start": v(-70, 90) * mm, "end": v(70, 90) * mm});
            skPoint(sketch, "E80", {"position": v(0, 90) * mm});
            skLineSegment(sketch, "E81", {"start": v(0, 90) * mm, "end": v(0, 120) * mm, "construction": true});
            skCircle(sketch, "E82", {"center": v(0, 120) * mm, "radius": 6 * mm});
            skLineSegment(sketch, "E83", {"start": v(-70, 90) * mm, "end": v(0, 90) * mm});
            skPoint(sketch, "E84", {"position": v(-35, 90) * mm});
            skLineSegment(sketch, "E85", {"start": v(0, 90) * mm, "end": v(70, 90) * mm});
            skPoint(sketch, "E86", {"position": v(35, 90) * mm});
            skLineSegment(sketch, "E87", {"start": v(0, 120) * mm, "end": v(6.9, 120) * mm});
            skLineSegment(sketch, "E88", {"start": v(-35, 90) * mm, "end": v(-17, 108) * mm});
            skLineSegment(sketch, "E89", {"start": v(-17, 108) * mm, "end": v(-17, 120) * mm});
            skLineSegment(sketch, "E90", {"start": v(35, 90) * mm, "end": v(36.97, 90) * mm});
            skLineSegment(sketch, "E91", {"start": v(35, 90) * mm, "end": v(17, 108) * mm});
            skLineSegment(sketch, "E92", {"start": v(17, 108) * mm, "end": v(17, 120) * mm});
            skPoint(sketch, "E92.endSnap0", {"position": v(3.45, 120) * mm});
            skArc(sketch, "E93", {"start": v(17, 120) * mm, "mid": v(0, 137) * mm, "end": v(-17, 120) * mm});
            skLineSegment(sketch, "E94", {"start": v(-80, 80) * mm, "end": v(-80, -60.8) * mm});
            skLineSegment(sketch, "E95", {"start": v(-70, -90) * mm, "end": v(60.48, -90) * mm});
            skLineSegment(sketch, "E96", {"start": v(80, 62.25) * mm, "end": v(80, -62.25) * mm});
            skLineSegment(sketch, "E97", {"start": v(80, 0) * mm, "end": v(-80, 0) * mm, "construction": true});
            skLineSegment(sketch, "E98.MirrorCS", {"start": v(-35, -90) * mm, "end": v(-17, -108) * mm});
            skLineSegment(sketch, "E99.MirrorCS", {"start": v(-17, -108) * mm, "end": v(-17, -120) * mm});
            skArc(sketch, "E100.MirrorCS", {"start": v(17, -120) * mm, "mid": v(0, -137) * mm, "end": v(-17, -120) * mm});
            skLineSegment(sketch, "E101.MirrorCS", {"start": v(17, -108) * mm, "end": v(17, -120) * mm});
            skLineSegment(sketch, "E102.MirrorCS", {"start": v(35, -90) * mm, "end": v(17, -108) * mm});
            skLineSegment(sketch, "E103.MirrorCS", {"start": v(0, -90) * mm, "end": v(0, -120) * mm, "construction": true});
            skCircle(sketch, "E104.MirrorC", {"center": v(0, -120) * mm, "radius": 6 * mm});
            skPoint(sketch, "E105", {"position": v(-60, 67.5) * mm});
            skPoint(sketch, "E106", {"position": v(60, 67.5) * mm});
            skPoint(sketch, "E107", {"position": v(60, -67.5) * mm});
            skPoint(sketch, "E108", {"position": v(-60, -67.5) * mm});
            skArc(sketch, "E109", {"start": v(56.15, 48.18) * mm, "mid": v(0, 61.5) * mm, "end": v(-56.15, 48.18) * mm});
            skArc(sketch, "E110", {"start": v(-52.05, -51.2) * mm, "mid": v(2.4, -61.92) * mm, "end": v(56.15, -48.18) * mm});
            skLineSegment(sketch, "E111", {"start": v(-60, 40.3) * mm, "end": v(-60, -40.3) * mm});
            skLineSegment(sketch, "E112", {"start": v(60, 40.3) * mm, "end": v(60, -40.3) * mm});
            skSolve(sketch);
        }
        {
            var Q0;
            {var subQ12=sQuery(id+"F16.wireOp",EDGE,"E90");Q0=makeQuery(id+"F16.imprint","IMPRINT",FACE,{"disambiguationData":[TD([[makeQuery(id+"F16.imprint","IMPRINT",EDGE,{"derivedFrom":subQ12}),-1.0]])]});}
            var Q1;
            Q1=makeQuery(id+"F16.imprint","IMPRINT",FACE,{"disambiguationData":[TD([[makeQuery(id+"F16.imprint","IMPRINT",EDGE,{"derivedFrom":sQuery(id+"F16.wireOp",EDGE,"E82")}),-1.0]])]});
            var Q2;
            {var subQ1=sQuery(id+"F16.wireOp",EDGE,"E98.MirrorCS");Q2=makeQuery(id+"F16.imprint","IMPRINT",FACE,{"disambiguationData":[TD([[makeQuery(id+"F16.imprint","IMPRINT",EDGE,{"derivedFrom":subQ1}),1.0]])]});}
            var Q3;
            {var subQ0=sQuery(id+"F4.wireOp",EDGE,"E63.0.MirrorCS");var subQ1=sQuery(id+"F4.wireOp",EDGE,"E62.0.MirrorCS");var subQ2=sQuery(id+"F4.wireOp",EDGE,"E61.0.MirrorCS");var subQ3=sQuery(id+"F4.wireOp",EDGE,"E60.0.MirrorCS");var subQ4=sQuery(id+"F4.wireOp",EDGE,"E59.0.MirrorCS");var subQ5=sQuery(id+"F4.wireOp",EDGE,"E58.0.MirrorCS");var subQ6=sQuery(id+"F4.wireOp",EDGE,"E57.0.MirrorCS");var subQ7=sQuery(id+"F4.wireOp",EDGE,"E56.0.MirrorCS");var subQ8=sQuery(id+"F4.wireOp",EDGE,"E55.0.MirrorCS");var subQ9=sQuery(id+"F4.wireOp",EDGE,"E54.0.MirrorCS");var subQ10=sQuery(id+"F4.wireOp",EDGE,"E53.0.MirrorCS");var subQ11=sQuery(id+"F4.wireOp",EDGE,"E52.filletArc");var subQ12=sQuery(id+"F4.wireOp",EDGE,"E45");var subQ13=sQuery(id+"F4.wireOp",EDGE,"E43");var subQ14=sQuery(id+"F4.wireOp",EDGE,"E42");var subQ15=sQuery(id+"F4.wireOp",EDGE,"E41");var subQ16=sQuery(id+"F4.wireOp",EDGE,"E46");var subQ17=sQuery(id+"F4.wireOp",EDGE,"E47.filletArc");var subQ18=sQuery(id+"F4.wireOp",EDGE,"E48.filletArc");var subQ19=sQuery(id+"F4.wireOp",EDGE,"E49.filletArc");var subQ20=sQuery(id+"F4.wireOp",EDGE,"E50.filletArc");var subQ21=sQuery(id+"F4.wireOp",EDGE,"E51.filletArc");Q3=makeQuery(id+"F6.boolean.opBoolean","SPLIT",FACE,{"disambiguationData":[TD([makeQuery(id+"F5.opExtrude","SWEPT_FACE",FACE,{"disambiguationData":[OSD([subQ15])]})])],"derivedFrom":makeQuery(id+"F5.opExtrude","CAP_FACE",FACE,{"disambiguationData":[OSD([sQuery(id+"F4.wireOp",EDGE,"E27.0"),sQuery(id+"F4.wireOp",EDGE,"E28.0"),sQuery(id+"F4.wireOp",EDGE,"E29"),sQuery(id+"F4.wireOp",EDGE,"E30"),sQuery(id+"F4.wireOp",EDGE,"E33.filletArc"),sQuery(id+"F4.wireOp",EDGE,"E34.filletArc"),sQuery(id+"F4.wireOp",EDGE,"E35.filletArc"),sQuery(id+"F4.wireOp",EDGE,"E36.filletArc"),subQ15,subQ14,subQ13,subQ12,subQ16,subQ17,subQ18,subQ19,subQ20,subQ21,subQ11,subQ10,subQ9,subQ8,subQ7,subQ6,subQ5,subQ4,subQ3,subQ2,subQ1,subQ0])],"isStart":true})});}
            extrude(context, id + "F17", {"entities" : qUnion([Q0, Q1, Q2]), "endBound" : BoundingType.UP_TO_SURFACE, "endBoundEntityFace" : qUnion([Q3]), "depth" : 25 * mm});
        }
    });
